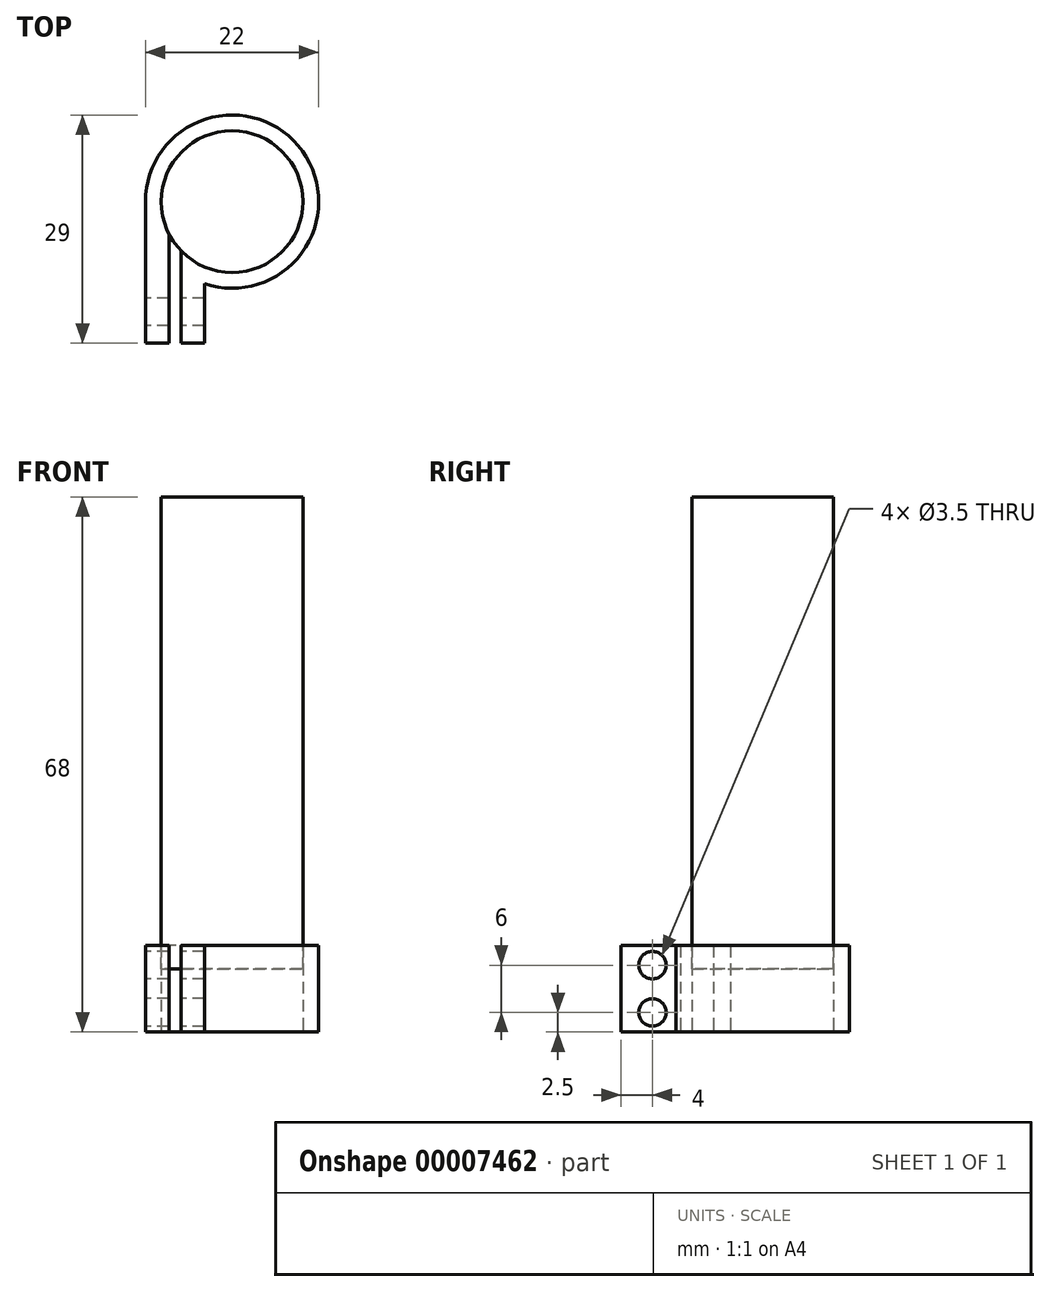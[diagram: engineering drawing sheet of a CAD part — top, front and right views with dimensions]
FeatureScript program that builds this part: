
annotation { "Feature Type Name" : "Feature", "Feature Type Description" : "" }
export const myFeature = defineFeature(function(context is Context, id is Id, definition is map)
    precondition{}
    {
        {
            var Q0;
            Q0=qCreatedBy(makeId("Front.planeOp"),FACE);
            var sketch = newSketch(context, id + "F0", { "sketchPlane" : qUnion([Q0])});
            skLineSegment(sketch, "E0", {"start": v(0, 0) * mm, "end": v(0, 8) * mm, "construction": true});
            skLineSegment(sketch, "E1", {"start": v(0, 8) * mm, "end": v(9, 8) * mm});
            skLineSegment(sketch, "E2", {"start": v(9, 8) * mm, "end": v(9, 68) * mm});
            skLineSegment(sketch, "E3", {"start": v(9, 68) * mm, "end": v(0, 68) * mm});
            skLineSegment(sketch, "E4", {"start": v(0, 68) * mm, "end": v(0, 8) * mm});
            skSolve(sketch);
        }
        {
            var Q0;
            Q0=makeQuery(id+"F0.imprint","IMPRINT",FACE,{"disambiguationData":[TD([[makeQuery(id+"F0.imprint","IMPRINT",EDGE,{"derivedFrom":sQuery(id+"F0.wireOp",EDGE,"E1")}),1.0]])]});
            var Q1;
            Q1=sQuery(id+"F0.wireOp",EDGE,"E4");
            revolve(context, id + "F1", {"entities" : qUnion([Q0]), "axis" : qUnion([Q1]), "revolveType" : RevolveType.FULL});
        }
        {
            var Q0;
            Q0=qCreatedBy(makeId("Top.planeOp"),FACE);
            var sketch = newSketch(context, id + "F2", { "sketchPlane" : qUnion([Q0])});
            skLineSegment(sketch, "E5", {"start": v(-11, -18) * mm, "end": v(-11, 0) * mm});
            skCircle(sketch, "E6", {"center": v(0, 0) * mm, "radius": 9 * mm});
            skCircle(sketch, "E7", {"center": v(0, 0) * mm, "radius": 11 * mm});
            skLineSegment(sketch, "E8", {"start": v(-11, -18) * mm, "end": v(-8, -18) * mm});
            skLineSegment(sketch, "E9", {"start": v(-8, -18) * mm, "end": v(-8, -4.12) * mm});
            skLineSegment(sketch, "E10", {"start": v(-6.5, -6.22) * mm, "end": v(-6.5, -18) * mm});
            skLineSegment(sketch, "E11", {"start": v(-6.5, -18) * mm, "end": v(-3.5, -18) * mm});
            skLineSegment(sketch, "E12", {"start": v(-3.5, -18) * mm, "end": v(-3.5, -8.3) * mm});
            skLineSegment(sketch, "E13", {"start": v(0, 0) * mm, "end": v(0, -11) * mm, "construction": true});
            skLineSegment(sketch, "E14", {"start": v(-6.5, -18) * mm, "end": v(-8, -18) * mm, "construction": true});
            skSolve(sketch);
        }
        {
            var Q0;
            {var subQ3=sQuery(id+"F2.wireOp",EDGE,"E11");Q0=makeQuery(id+"F2.imprint","IMPRINT",FACE,{"disambiguationData":[TD([[makeQuery(id+"F2.imprint","IMPRINT",EDGE,{"derivedFrom":subQ3}),1.0]])]});}
            var Q1;
            {var subQ3=sQuery(id+"F2.wireOp",EDGE,"E6");var subQ5=sQuery(id+"F2.wireOp",EDGE,"E10");var subQ7=makeQuery(id+"F2.imprint","INTERSECT",VERTEX,{"derivedFrom":[subQ3,subQ5]});Q1=makeQuery(id+"F2.imprint","IMPRINT",FACE,{"disambiguationData":[TD([[makeQuery(id+"F2.imprint","IMPRINT",EDGE,{"disambiguationData":[TD([[subQ7,-1.0]])],"derivedFrom":subQ3}),-1.0]])]});}
            var Q2;
            {var subQ3=sQuery(id+"F2.wireOp",EDGE,"E6");var subQ5=sQuery(id+"F2.wireOp",EDGE,"E9");var subQ6=makeQuery(id+"F2.imprint","INTERSECT",VERTEX,{"derivedFrom":[subQ3,subQ5]});Q2=makeQuery(id+"F2.imprint","IMPRINT",FACE,{"disambiguationData":[TD([[makeQuery(id+"F2.imprint","IMPRINT",EDGE,{"disambiguationData":[TD([[subQ6,1.0]])],"derivedFrom":subQ3}),-1.0]])]});}
            var Q3;
            {var subQ3=sQuery(id+"F2.wireOp",EDGE,"E5");Q3=makeQuery(id+"F2.imprint","IMPRINT",FACE,{"disambiguationData":[TD([[makeQuery(id+"F2.imprint","IMPRINT",EDGE,{"derivedFrom":subQ3}),-1.0]])]});}
            extrude(context, id + "F3", {"entities" : qUnion([Q0, Q1, Q2, Q3]), "depth" : 11 * mm});
        }
        {
            var Q0;
            Q0=makeQuery(id+"F3.opExtrude","SWEPT_FACE",FACE,{"disambiguationData":[OSD([sQuery(id+"F2.wireOp",EDGE,"E5")])]});
            var sketch = newSketch(context, id + "F4", { "sketchPlane" : qUnion([Q0])});
            skLineSegment(sketch, "E15.0", {"start": v(18, 11) * mm, "end": v(18, 0) * mm});
            skLineSegment(sketch, "E16", {"start": v(18, 0) * mm, "end": v(14, 0) * mm, "construction": true});
            skLineSegment(sketch, "E17", {"start": v(14, 0) * mm, "end": v(14, 2.5) * mm, "construction": true});
            skLineSegment(sketch, "E18", {"start": v(14, 2.5) * mm, "end": v(14, 8.5) * mm, "construction": true});
            skCircle(sketch, "E19", {"center": v(14, 8.5) * mm, "radius": 1.75 * mm});
            skCircle(sketch, "E20", {"center": v(14, 2.5) * mm, "radius": 1.75 * mm});
            skSolve(sketch);
        }
        {
            var Q0;
            Q0 = qSketchRegion(id + "F4", true);
            extrude(context, id + "F5", {"entities" : qUnion([Q0]), "operationType" : NewBodyOperationType.REMOVE, "oppositeDirection" : true, "depth" : 25 * mm});
        }
    });
